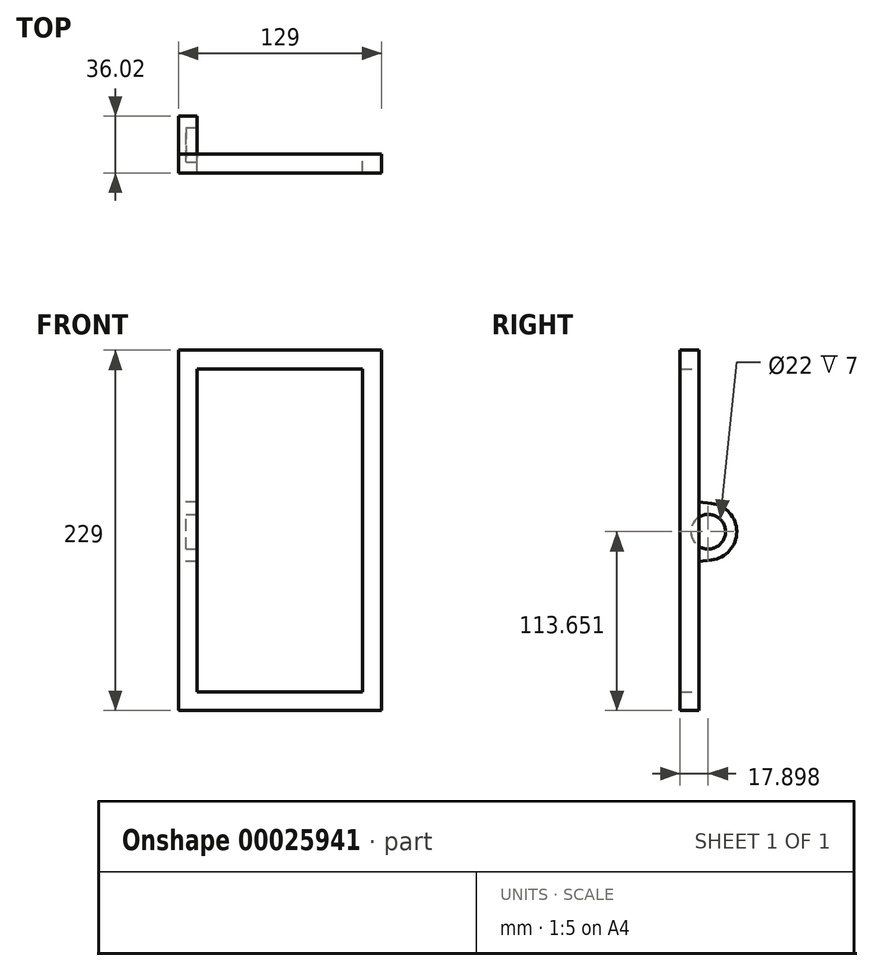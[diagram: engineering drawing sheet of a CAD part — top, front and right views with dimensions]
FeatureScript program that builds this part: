
annotation { "Feature Type Name" : "Feature", "Feature Type Description" : "" }
export const myFeature = defineFeature(function(context is Context, id is Id, definition is map)
    precondition{}
    {
        {
            var Q0;
            Q0=qCreatedBy(makeId("Front.planeOp"),FACE);
            var sketch = newSketch(context, id + "F0", { "sketchPlane" : qUnion([Q0])});
            skLineSegment(sketch, "E0.rect.bottom", {"start": v(-52.5, 102.5) * mm, "end": v(52.5, 102.5) * mm});
            skLineSegment(sketch, "E0.rect.top", {"start": v(-52.5, -102.5) * mm, "end": v(52.5, -102.5) * mm});
            skLineSegment(sketch, "E0.rect.left", {"start": v(-52.5, 102.5) * mm, "end": v(-52.5, -102.5) * mm});
            skLineSegment(sketch, "E0.rect.right", {"start": v(52.5, 102.5) * mm, "end": v(52.5, -102.5) * mm});
            skPoint(sketch, "E0.rect.middle", {"position": v(0, 0) * mm});
            skLineSegment(sketch, "E1.rect.bottom", {"start": v(-64.5, 114.5) * mm, "end": v(64.5, 114.5) * mm});
            skLineSegment(sketch, "E1.rect.top", {"start": v(-64.5, -114.5) * mm, "end": v(64.5, -114.5) * mm});
            skLineSegment(sketch, "E1.rect.left", {"start": v(-64.5, 114.5) * mm, "end": v(-64.5, -114.5) * mm});
            skLineSegment(sketch, "E1.rect.right", {"start": v(64.5, 114.5) * mm, "end": v(64.5, -114.5) * mm});
            skSolve(sketch);
        }
        {
            var Q0;
            Q0=makeQuery(id+"F0.imprint","IMPRINT",FACE,{"disambiguationData":[TD([[makeQuery(id+"F0.imprint","IMPRINT",EDGE,{"derivedFrom":sQuery(id+"F0.wireOp",EDGE,"E0.rect.bottom")}),1.0]])]});
            extrude(context, id + "F1", {"entities" : qUnion([Q0]), "depth" : 12 * mm, "symmetric" : true});
        }
        {
            var Q0;
            Q0=makeQuery(id+"F1.opExtrude","SWEPT_FACE",FACE,{"disambiguationData":[OSD([sQuery(id+"F0.wireOp",EDGE,"E1.rect.left")])]});
            var sketch = newSketch(context, id + "F2", { "sketchPlane" : qUnion([Q0])});
            skLineSegment(sketch, "E2.bottom", {"start": v(6, 17.15) * mm, "end": v(-30, 17.15) * mm, "construction": true});
            skLineSegment(sketch, "E2.top", {"start": v(6, -18.85) * mm, "end": v(-30, -18.85) * mm, "construction": true});
            skLineSegment(sketch, "E2.left", {"start": v(6, 17.15) * mm, "end": v(6, -18.85) * mm, "construction": true});
            skLineSegment(sketch, "E2.right", {"start": v(-30, 17.15) * mm, "end": v(-30, -18.85) * mm, "construction": true});
            skPoint(sketch, "E3.first.point", {"position": v(-30, 0) * mm});
            skPoint(sketch, "E3.second.point", {"position": v(-12, 17.15) * mm});
            skPoint(sketch, "E3.third.point", {"position": v(-12, -18.85) * mm});
            skPoint(sketch, "E4", {"position": v(-14, 17.15) * mm});
            skPoint(sketch, "E5", {"position": v(-14, -18.85) * mm});
            skArc(sketch, "E6", {"start": v(-14, 17.15) * mm, "mid": v(-30.02, -0.85) * mm, "end": v(-14, -18.85) * mm});
            skLineSegment(sketch, "E7", {"start": v(-14, 17.15) * mm, "end": v(-6, 18.09) * mm});
            skLineSegment(sketch, "E8", {"start": v(-14, -18.85) * mm, "end": v(-6, -19.78) * mm});
            skLineSegment(sketch, "E9", {"start": v(-6, -19.78) * mm, "end": v(-6, 18.09) * mm});
            skSolve(sketch);
        }
        {
            var Q0;
            Q0=makeQuery(id+"F2.imprint","IMPRINT",FACE,{"disambiguationData":[TD([[makeQuery(id+"F2.imprint","IMPRINT",EDGE,{"derivedFrom":sQuery(id+"F2.wireOp",EDGE,"E6")}),1.0]])]});
            var Q1;
            Q1=makeQuery(id+"F1.opExtrude","SWEPT_FACE",FACE,{"disambiguationData":[OSD([sQuery(id+"F0.wireOp",EDGE,"E0.rect.left")])]});
            extrude(context, id + "F3", {"entities" : qUnion([Q0]), "operationType" : NewBodyOperationType.ADD, "endBound" : BoundingType.UP_TO_SURFACE, "oppositeDirection" : true, "endBoundEntityFace" : qUnion([Q1]), "depth" : 25 * mm});
        }
        {
            var Q0;
            Q0=makeQuery(id+"F3.boolean.opBoolean","MERGE",FACE,{"derivedFrom":[makeQuery(id+"F1.opExtrude","SWEPT_FACE",FACE,{"disambiguationData":[OSD([sQuery(id+"F0.wireOp",EDGE,"E0.rect.left")])]}),makeQuery(id+"F3.opExtrude","CAP_FACE",FACE,{"disambiguationData":[OSD([sQuery(id+"F2.wireOp",EDGE,"E6"),sQuery(id+"F2.wireOp",EDGE,"E7"),sQuery(id+"F2.wireOp",EDGE,"E8"),sQuery(id+"F2.wireOp",EDGE,"E9")])],"isStart":false})]});
            var sketch = newSketch(context, id + "F4", { "sketchPlane" : qUnion([Q0])});
            skCircle(sketch, "E10", {"center": v(11.9, -0.85) * mm, "radius": 11 * mm});
            skSolve(sketch);
        }
        {
            var Q0;
            Q0 = qSketchRegion(id + "F4", true);
            extrude(context, id + "F5", {"entities" : qUnion([Q0]), "operationType" : NewBodyOperationType.REMOVE, "oppositeDirection" : true, "depth" : 7 * mm});
        }
    });
